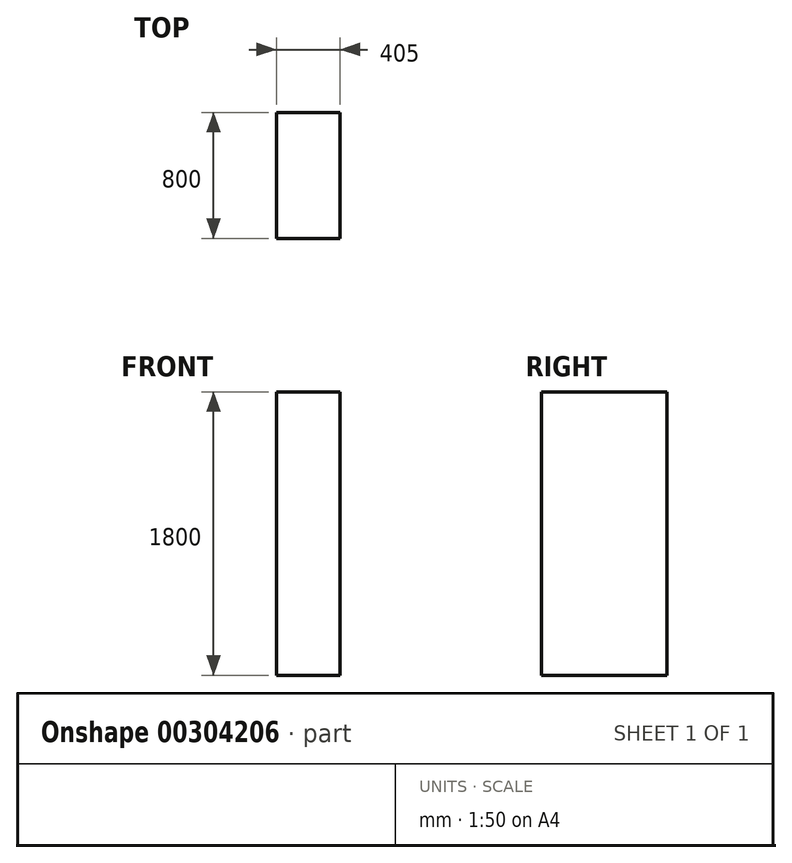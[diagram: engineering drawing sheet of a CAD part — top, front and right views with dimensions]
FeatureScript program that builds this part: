
annotation { "Feature Type Name" : "Feature", "Feature Type Description" : "" }
export const myFeature = defineFeature(function(context is Context, id is Id, definition is map)
    precondition{}
    {
        {
            var Q0;
            Q0=qCreatedBy(makeId("Top.planeOp"),FACE);
            var sketch = newSketch(context, id + "F0", { "sketchPlane" : qUnion([Q0])});
            skLineSegment(sketch, "E0.bottom", {"start": v(0, 0) * mm, "end": v(405, 0) * mm});
            skLineSegment(sketch, "E0.top", {"start": v(0, 800) * mm, "end": v(405, 800) * mm});
            skLineSegment(sketch, "E0.left", {"start": v(0, 0) * mm, "end": v(0, 800) * mm});
            skLineSegment(sketch, "E0.right", {"start": v(405, 0) * mm, "end": v(405, 800) * mm});
            skSolve(sketch);
        }
        {
            var Q0;
            Q0 = qSketchRegion(id + "F0", true);
            var Q1;
            Q1 = qConstructionFilter(qBodyType(qCreatedBy(id + "F0" ,EDGE), BodyType.WIRE), ConstructionObject.NO);
            extrude(context, id + "F1", {"entities" : qUnion([Q0]), "surfaceEntities" : qUnion([Q1]), "depth" : 1800 * mm});
        }
    });
